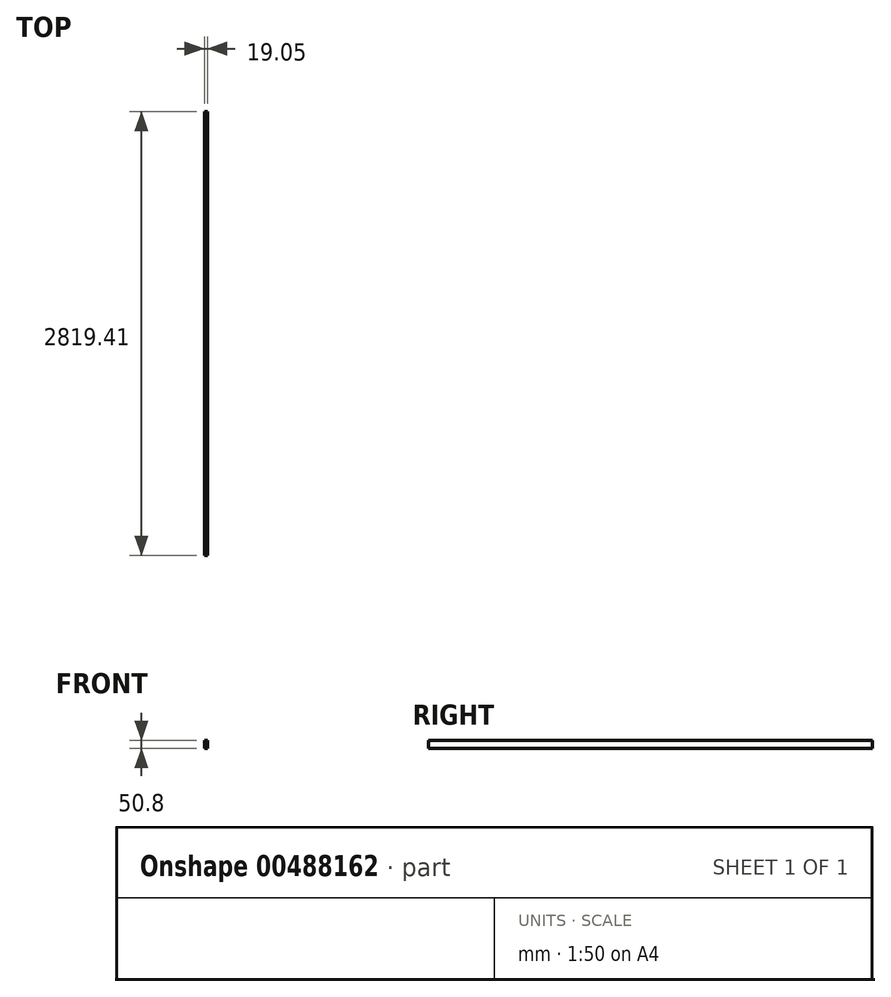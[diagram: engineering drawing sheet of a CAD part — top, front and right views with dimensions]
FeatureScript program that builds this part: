
annotation { "Feature Type Name" : "Feature", "Feature Type Description" : "" }
export const myFeature = defineFeature(function(context is Context, id is Id, definition is map)
    precondition{}
    {
        {
            var Q0;
            Q0=qCreatedBy(makeId("Front.planeOp"),FACE);
            var sketch = newSketch(context, id + "F0", { "sketchPlane" : qUnion([Q0])});
            skLineSegment(sketch, "E0", {"start": v(0, 0) * mm, "end": v(19.05, 0) * mm});
            skLineSegment(sketch, "E1", {"start": v(0, 0) * mm, "end": v(0, -50.8) * mm});
            skLineSegment(sketch, "E2", {"start": v(0, -50.8) * mm, "end": v(19.05, -50.8) * mm});
            skLineSegment(sketch, "E3", {"start": v(19.05, -50.8) * mm, "end": v(19.05, 0) * mm});
            skSolve(sketch);
        }
        {
            var Q0;
            Q0=makeQuery(id+"F0.imprint","IMPRINT",FACE,{"disambiguationData":[TD([[makeQuery(id+"F0.imprint","IMPRINT",EDGE,{"derivedFrom":sQuery(id+"F0.wireOp",EDGE,"E0")}),-1.0]])]});
            extrude(context, id + "F1", {"entities" : qUnion([Q0]), "depth" : 2743.2 * mm + 76.2 * mm + 1 / 76.2 * mm, "offsetDistance" : 25.4 * mm});
        }
    });
